# Revit family: Eurolan_Вертикальный организатор Zero-U
name_source: partatom
category: Устройства связи
units: mm (PartAtom-declared; Revit-internal decimal feet)

## family parameters
Всегда вертикально = Да
На основе рабочей плоскости = Нет
Общий = Нет
При загрузке вырезать с полостями = Нет
Размер круглого соединителя = Использовать диаметр
Сохранять ориентацию аннотаций = Нет
Тип детали = Нормальный
Точка расчета площади = Нет

## types (2) — shared parameters
ADSK_Единица измерения = шт
ADSK_Завод-изготовитель = Eurolan
ADSK_Количество = 1
ADSK_Материал = RAL 9005
ADSK_Наименование краткое = Вертикальный организатор Zero-U
zero-valued in all types: ADSK_Масса

## per-type parameters (varying)
| type | ADSK_Код изделия | ADSK_Марка | ADSK_Наименование | Выбор_геометри |
| Zero-U_4U | 60A-18-04-16-09BL | 4U | Вертикальный организатор Zero-U, 4U, с пластиковыми пальцами | Вертикальный организатор Zero-U, 4U : 4U |
| Zero-U_6U | 60A-18-06-16-09BL | 6U | Вертикальный организатор Zero-U, 6U, с пластиковыми пальцами | Вертикальный организатор Zero-U, 6U : 6U |
